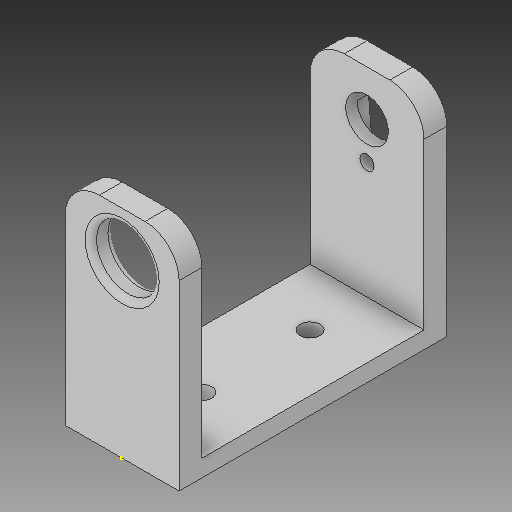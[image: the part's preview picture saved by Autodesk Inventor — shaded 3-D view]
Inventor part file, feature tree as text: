
AUTODESK INVENTOR PART (.ipt)
format: ipt  version: 2019 (Build 230136000, 136)  size: 213,504 bytes
history: native  units: mm
features: sketch x8, projected_geometry x6, hole x4, extrude x3, fillet x3
ambient origin geometry x8: Origin, YZ Plane, XZ Plane, XY Plane, X Axis, Y Axis, Z Axis, Center Point
bodies: Solid1 (feature_tree)
feature tree (24):
  extrude  "Extrusion1"  Depth=20.0mm
  extrude  "Extrusion2"  Depth=4.0mm
  sketch  "Sketch3"  dims[d5=4.0mm d6=35.0mm d7=0.0mm d8=10.0mm]
  hole  "Hole1"  [1 undecoded]
  fillet  "Fillet1"  Radius=10.0mm
  hole  "Hole3"  [1 undecoded]
  extrude  "Extrusion4"  Depth=10.0mm
  hole  "Hole4"  [1 undecoded]
  hole  "Hole5"  [1 undecoded]
  fillet  "Fillet2"  Radius=10.0mm
  fillet  "Fillet3"  Radius=2.0mm
  sketch  "Sketch1"  dims[d0=47.0mm d1=20.0mm]
  sketch  "Sketch2"  dims[d2=3.0mm d3=0.0mm d4=4.0mm]
  projected_geometry  "Projected Loop1"
  sketch  "Sketch4"  dims[d9=8.0mm]
  projected_geometry  "Projected Loop2"
  sketch  "Sketch8"  dims[d10=11.0mm d11=6.0mm d12=4.0mm d13=2.0mm d14=90.0deg d15=8.0mm d16=0.0mm d36=6.0mm]
  projected_geometry  "Projected Loop5"
  sketch  "Sketch10"  dims[d37=10.0mm d38=10.0mm]
  projected_geometry  "Projected Loop7"
  sketch  "Sketch11"  dims[d39=3.5mm d40=6.0mm d41=4.0mm d42=2.0mm d43=90.0deg d44=8.0mm d45=0.0mm d47=16.5mm]
  projected_geometry  "Projected Loop8"
  sketch  "Sketch12"  dims[d48=7.5mm d49=5.0mm d50=10.0mm d51=2.0mm d52=2.0mm d53=8.0mm d54=8.0mm d55=2.0mm d56=0.0mm d57=7.5mm d58=6.0mm d59=4.0mm d60=2.0mm d61=90.0deg d62=8.0mm d63=0.0mm d64=6.5mm d65=10.0mm d66=2.5mm d67=6.0mm d68=4.0mm d69=2.0mm d70=90.0deg d71=8.0mm d72=0.0mm d73=1.0mm d74=1.0mm d75=19.0mm]
  projected_geometry  "Projected Loop9"
note: 4 required parameter values undecoded (feature->parameter linkage not recoverable at this tier; creation-order binding heuristic only, values carry confidence <= 0.55)
